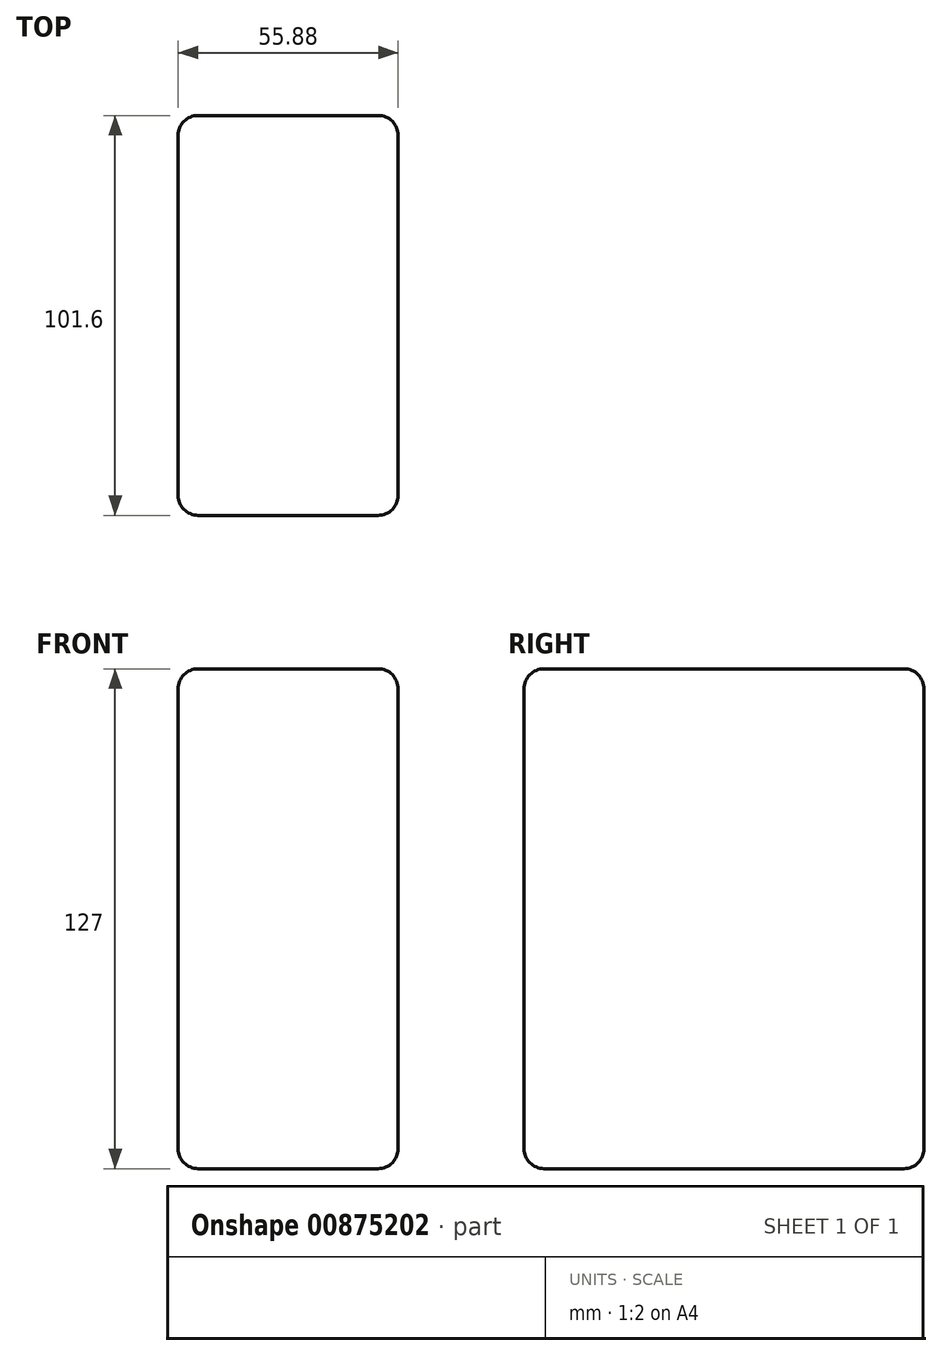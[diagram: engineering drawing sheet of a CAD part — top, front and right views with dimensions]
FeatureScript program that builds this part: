
annotation { "Feature Type Name" : "Feature", "Feature Type Description" : "" }
export const myFeature = defineFeature(function(context is Context, id is Id, definition is map)
    precondition{}
    {
        {
            var Q0;
            Q0=qCreatedBy(makeId("Right.planeOp"),FACE);
            var sketch = newSketch(context, id + "F0", { "sketchPlane" : qUnion([Q0])});
            skLineSegment(sketch, "E0.bottom", {"start": v(-50.8, 63.5) * mm, "end": v(50.8, 63.5) * mm});
            skLineSegment(sketch, "E0.top", {"start": v(-50.8, -63.5) * mm, "end": v(50.8, -63.5) * mm});
            skLineSegment(sketch, "E0.left", {"start": v(-50.8, 63.5) * mm, "end": v(-50.8, -63.5) * mm});
            skLineSegment(sketch, "E0.right", {"start": v(50.8, 63.5) * mm, "end": v(50.8, -63.5) * mm});
            skPoint(sketch, "E0.middle", {"position": v(0, 0) * mm});
            skSolve(sketch);
        }
        {
            var Q0;
            Q0=makeQuery(id+"F0.imprint","IMPRINT",FACE,{"disambiguationData":[TD([[makeQuery(id+"F0.imprint","IMPRINT",EDGE,{"derivedFrom":sQuery(id+"F0.wireOp",EDGE,"E0.bottom")}),-1.0]])]});
            extrude(context, id + "F1", {"entities" : qUnion([Q0]), "depth" : 55.88 * mm, "offsetDistance" : 25.4 * mm});
        }
        {
            var Q0;
            Q0=makeQuery(id+"F1.opExtrude","SWEPT_FACE",FACE,{"disambiguationData":[OSD([sQuery(id+"F0.wireOp",EDGE,"E0.bottom")])]});
            var Q1;
            Q1=makeQuery(id+"F1.opExtrude","SWEPT_FACE",FACE,{"disambiguationData":[OSD([sQuery(id+"F0.wireOp",EDGE,"E0.left")])]});
            var Q2;
            Q2=makeQuery(id+"F1.opExtrude","CAP_FACE",FACE,{"disambiguationData":[OSD([sQuery(id+"F0.wireOp",EDGE,"E0.bottom"),sQuery(id+"F0.wireOp",EDGE,"E0.top"),sQuery(id+"F0.wireOp",EDGE,"E0.left"),sQuery(id+"F0.wireOp",EDGE,"E0.right")])],"isStart":false});
            var Q3;
            Q3=makeQuery(id+"F1.opExtrude","SWEPT_FACE",FACE,{"disambiguationData":[OSD([sQuery(id+"F0.wireOp",EDGE,"E0.top")])]});
            var Q4;
            Q4=makeQuery(id+"F1.opExtrude","CAP_FACE",FACE,{"disambiguationData":[OSD([sQuery(id+"F0.wireOp",EDGE,"E0.bottom"),sQuery(id+"F0.wireOp",EDGE,"E0.top"),sQuery(id+"F0.wireOp",EDGE,"E0.left"),sQuery(id+"F0.wireOp",EDGE,"E0.right")])],"isStart":true});
            var Q5;
            Q5=makeQuery(id+"F1.opExtrude","SWEPT_FACE",FACE,{"disambiguationData":[OSD([sQuery(id+"F0.wireOp",EDGE,"E0.right")])]});
            fillet(context, id + "F2", {"entities" : qUnion([Q0, Q1, Q2, Q3, Q4, Q5]), "radius" : 5.08 * mm, "tangentPropagation" : true, "allowEdgeOverflow" : false});
        }
    });
